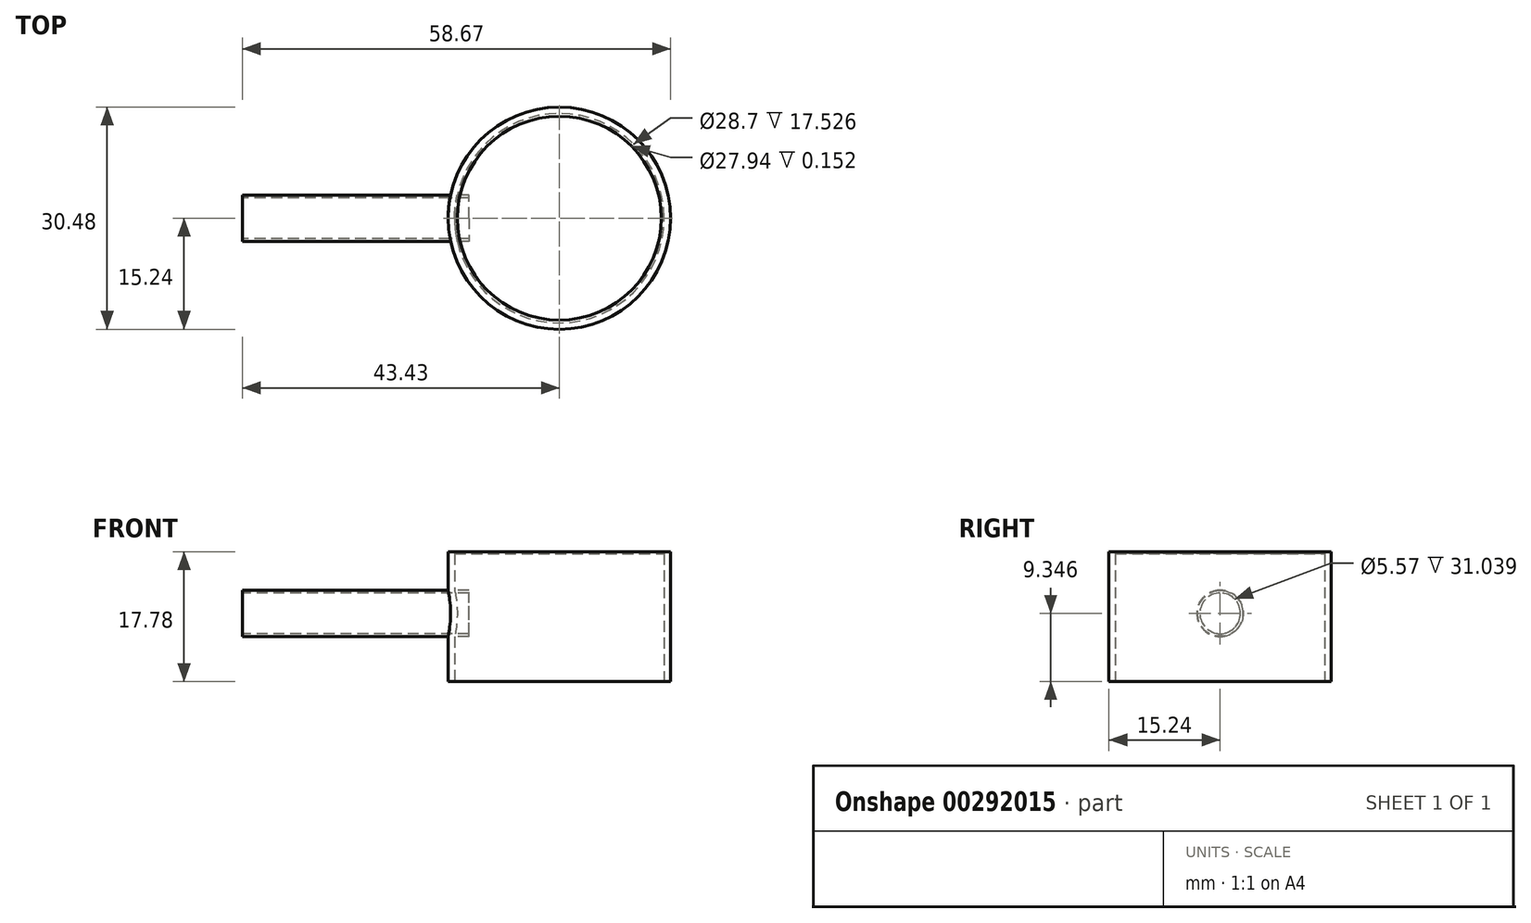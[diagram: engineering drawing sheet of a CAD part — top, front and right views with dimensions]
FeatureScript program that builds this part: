
annotation { "Feature Type Name" : "Feature", "Feature Type Description" : "" }
export const myFeature = defineFeature(function(context is Context, id is Id, definition is map)
    precondition{}
    {
        {
            var Q0;
            Q0=qCreatedBy(makeId("Top.planeOp"),FACE);
            var sketch = newSketch(context, id + "F0", { "sketchPlane" : qUnion([Q0])});
            skCircle(sketch, "E0", {"center": v(0, 0) * mm, "radius": 15.24 * mm});
            skSolve(sketch);
        }
        {
            var Q0;
            Q0=makeQuery(id+"F0.imprint","IMPRINT",FACE,{"disambiguationData":[TD([[makeQuery(id+"F0.imprint","IMPRINT",EDGE,{"derivedFrom":sQuery(id+"F0.wireOp",EDGE,"E0")}),1.0]])]});
            extrude(context, id + "F1", {"entities" : qUnion([Q0]), "depth" : 17.78 * mm});
        }
        {
            var Q0;
            Q0=makeQuery(id+"F1.opExtrude","CAP_FACE",FACE,{"disambiguationData":[OSD([sQuery(id+"F0.wireOp",EDGE,"E0")])],"isStart":true});
            var sketch = newSketch(context, id + "F2", { "sketchPlane" : qUnion([Q0])});
            skCircle(sketch, "E1", {"center": v(0, 0) * mm, "radius": 14.35 * mm});
            skSolve(sketch);
        }
        {
            var Q0;
            Q0=makeQuery(id+"F2.imprint","IMPRINT",FACE,{"disambiguationData":[TD([[makeQuery(id+"F2.imprint","IMPRINT",EDGE,{"derivedFrom":sQuery(id+"F2.wireOp",EDGE,"E1")}),1.0]])]});
            extrude(context, id + "F3", {"entities" : qUnion([Q0]), "operationType" : NewBodyOperationType.REMOVE, "oppositeDirection" : true, "depth" : 17.53 * mm});
        }
        {
            var Q0;
            Q0=qCreatedBy(makeId("Right.planeOp"),FACE);
            cPlane(context, id + "F4", {"entities" : qUnion([Q0]), "cplaneType" : CPlaneType.OFFSET, "offset" : 37.6 * mm, "oppositeDirection" : true, "width" : 152.4 * mm, "height" : 152.4 * mm});
        }
        {
            var Q0;
            Q0=qCreatedBy(id+"F4.planeOp",FACE);
            var sketch = newSketch(context, id + "F5", { "sketchPlane" : qUnion([Q0])});
            skCircle(sketch, "E2", {"center": v(0, 9.35) * mm, "radius": 3.17 * mm});
            skSolve(sketch);
        }
        {
            var Q0;
            Q0=makeQuery(id+"F5.imprint","IMPRINT",FACE,{"disambiguationData":[TD([[makeQuery(id+"F5.imprint","IMPRINT",EDGE,{"derivedFrom":sQuery(id+"F5.wireOp",EDGE,"E2")}),1.0]])]});
            extrude(context, id + "F6", {"entities" : qUnion([Q0]), "operationType" : NewBodyOperationType.ADD, "depth" : 25.2 * mm});
        }
        {
            var Q0;
            Q0=makeQuery(id+"F6.opExtrude","CAP_FACE",FACE,{"disambiguationData":[OSD([sQuery(id+"F5.wireOp",EDGE,"E2")])],"isStart":true});
            extrude(context, id + "F7", {"entities" : qUnion([Q0]), "operationType" : NewBodyOperationType.ADD, "depth" : 5.84 * mm});
        }
        {
            var Q0;
            Q0=makeQuery(id+"F7.opExtrude","CAP_FACE",FACE,{"disambiguationData":[OSD([sQuery(id+"F5.wireOp",EDGE,"E2")])],"isStart":false});
            var sketch = newSketch(context, id + "F8", { "sketchPlane" : qUnion([Q0])});
            skCircle(sketch, "E3", {"center": v(0, 9.35) * mm, "radius": 2.79 * mm});
            skSolve(sketch);
        }
        {
            var Q0;
            Q0=makeQuery(id+"F8.imprint","IMPRINT",FACE,{"disambiguationData":[TD([[makeQuery(id+"F8.imprint","IMPRINT",EDGE,{"derivedFrom":sQuery(id+"F8.wireOp",EDGE,"E3")}),1.0]])]});
            extrude(context, id + "F9", {"entities" : qUnion([Q0]), "operationType" : NewBodyOperationType.REMOVE, "oppositeDirection" : true, "depth" : 33.5 * mm});
        }
        {
            var Q0;
            Q0=makeQuery(id+"FdeeQY5tF3q5bJf_1.opExtrude","CAP_FACE",FACE,{"disambiguationData":[OSD([sQuery(id+"FjuaWUZXpRPCm27_1.wireOp",EDGE,"9ifgUn2c-6InR-MsKs-YUdc-CpAf7izLrKc4.bottom"),sQuery(id+"FjuaWUZXpRPCm27_1.wireOp",EDGE,"9ifgUn2c-6InR-MsKs-YUdc-CpAf7izLrKc4.top"),sQuery(id+"FjuaWUZXpRPCm27_1.wireOp",EDGE,"9ifgUn2c-6InR-MsKs-YUdc-CpAf7izLrKc4.left"),sQuery(id+"FjuaWUZXpRPCm27_1.wireOp",EDGE,"9ifgUn2c-6InR-MsKs-YUdc-CpAf7izLrKc4.right")])],"isStart":false});
            var sketch = newSketch(context, id + "F10", { "sketchPlane" : qUnion([Q0])});
            skLineSegment(sketch, "E4.bottom", {"start": v(-7.66, 2.5) * mm, "end": v(-4.2, 2.5) * mm});
            skLineSegment(sketch, "E4.top", {"start": v(-7.66, -2.5) * mm, "end": v(-4.2, -2.5) * mm});
            skLineSegment(sketch, "E4.left", {"start": v(-7.66, 2.5) * mm, "end": v(-7.66, -2.5) * mm});
            skLineSegment(sketch, "E4.right", {"start": v(-4.2, 2.5) * mm, "end": v(-4.2, -2.5) * mm});
            skPoint(sketch, "E4.middle", {"position": v(-5.93, 0) * mm});
            skSolve(sketch);
        }
        {
            var Q0;
            Q0=makeQuery(id+"F7sdj8080dzhA7E_1.opChamfer","BLEND_FACE",FACE,{"disambiguationData":[OSD([sQuery(id+"F10.wireOp",EDGE,"E4.left")])]});
            var sketch = newSketch(context, id + "F11", { "sketchPlane" : qUnion([Q0])});
            skCircle(sketch, "E5", {"center": v(0, 15.9) * mm, "radius": 1.4 * mm});
            skPoint(sketch, "E5.centerSnap0", {"position": v(2.5, 15.9) * mm});
            skSolve(sketch);
        }
        {
            var Q0;
            Q0=makeQuery(id+"F1.opExtrude","CAP_FACE",FACE,{"disambiguationData":[OSD([sQuery(id+"F0.wireOp",EDGE,"E0")])],"isStart":false});
            var sketch = newSketch(context, id + "F12", { "sketchPlane" : qUnion([Q0])});
            skCircle(sketch, "E6", {"center": v(0, 0) * mm, "radius": 13.97 * mm});
            skSolve(sketch);
        }
        {
            var Q0;
            Q0=makeQuery(id+"F12.imprint","IMPRINT",FACE,{"disambiguationData":[TD([[makeQuery(id+"F12.imprint","IMPRINT",EDGE,{"derivedFrom":sQuery(id+"F12.wireOp",EDGE,"E6")}),1.0]])]});
            extrude(context, id + "F13", {"entities" : qUnion([Q0]), "operationType" : NewBodyOperationType.ADD, "depth" : 0.46 * mm});
        }
        {
            var Q0;
            Q0=makeQuery(id+"F13.opExtrude","CAP_FACE",FACE,{"disambiguationData":[OSD([sQuery(id+"F12.wireOp",EDGE,"E6")])],"isStart":false});
            extrude(context, id + "F14", {"entities" : qUnion([Q0]), "operationType" : NewBodyOperationType.REMOVE, "oppositeDirection" : true, "depth" : 0.6 * mm});
        }
    });
